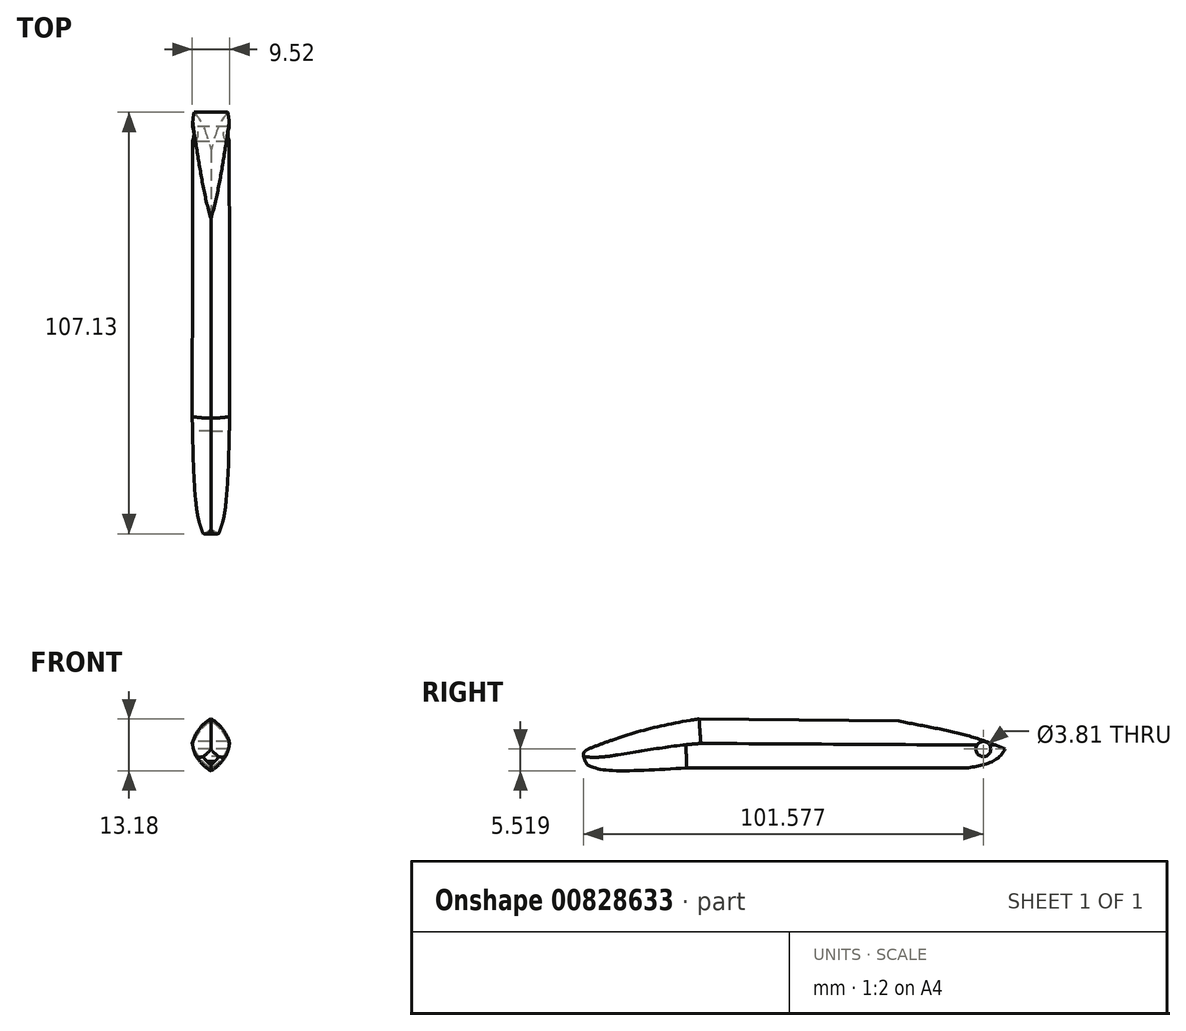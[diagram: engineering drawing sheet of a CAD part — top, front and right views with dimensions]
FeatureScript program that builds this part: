
annotation { "Feature Type Name" : "Feature", "Feature Type Description" : "" }
export const myFeature = defineFeature(function(context is Context, id is Id, definition is map)
    precondition{}
    {
        {
            var Q0;
            Q0=qCreatedBy(makeId("Right.planeOp"),FACE);
            var sketch = newSketch(context, id + "F0", { "sketchPlane" : qUnion([Q0])});
            skLineSegment(sketch, "E0.bottom", {"start": v(-19.6, 24.3) * mm, "end": v(31.2, 23.71) * mm});
            skFitSpline(sketch, "E1", {"points": [v(-19.6, 24.3) * mm, v(-36.26, 20.68) * mm, v(-47.72, 16.65) * mm], "startDerivative": vector(-31.96, -4.89) * mm, "endDerivative": vector(-23.37, -8.9) * mm});
            skFitSpline(sketch, "E2", {"points": [v(31.2, 23.71) * mm, v(49.24, 19.86) * mm, v(58.16, 16.65) * mm], "startDerivative": vector(33.9, -6.52) * mm, "endDerivative": vector(19.6, -7.94) * mm});
            skPoint(sketch, "E3.1.internal.orphan", {"position": v(55.44, 13.73) * mm});
            skFitSpline(sketch, "E4", {"points": [v(58.16, 16.65) * mm, v(55.44, 13.73) * mm, v(48.36, 11.81) * mm], "startDerivative": vector(-4.99, -9.02) * mm, "endDerivative": vector(-14.3, -2) * mm});
            skLineSegment(sketch, "E5", {"start": v(48.36, 11.81) * mm, "end": v(-22.76, 11.81) * mm});
            skFitSpline(sketch, "E6", {"points": [v(-47.95, 12.56) * mm, v(-43.68, 11.33) * mm, v(-22.76, 11.81) * mm], "startDerivative": vector(10.4, -4.36) * mm, "endDerivative": vector(35.02, 1.81) * mm});
            skFitSpline(sketch, "E7", {"points": [v(-47.95, 12.56) * mm, v(-48.51, 13.5) * mm], "startDerivative": vector(-0.94, 0.96) * mm, "endDerivative": vector(-0.94, 0.96) * mm});
            skFitSpline(sketch, "E8", {"points": [v(-47.72, 16.65) * mm, v(-48.91, 15.63) * mm, v(-48.51, 13.5) * mm], "startDerivative": vector(-3.65, -2.37) * mm, "endDerivative": vector(1.7, -4.5) * mm});
            skLineSegment(sketch, "E9", {"start": v(43.75, 21.22) * mm, "end": v(32.68, 11.81) * mm});
            skLineSegment(sketch, "E10", {"start": v(32.68, 11.81) * mm, "end": v(22.49, 23.81) * mm});
            skLineSegment(sketch, "E11", {"start": v(22.49, 23.81) * mm, "end": v(10.93, 11.81) * mm});
            skLineSegment(sketch, "E12", {"start": v(10.93, 11.81) * mm, "end": v(-1.82, 24.09) * mm});
            skLineSegment(sketch, "E13", {"start": v(-1.82, 24.09) * mm, "end": v(-13.64, 11.81) * mm});
            skLineSegment(sketch, "E14", {"start": v(-13.64, 11.81) * mm, "end": v(-21.92, 23.92) * mm});
            skLineSegment(sketch, "E15", {"start": v(-21.92, 23.92) * mm, "end": v(-30.76, 11.4) * mm});
            skLineSegment(sketch, "E16", {"start": v(-30.76, 11.4) * mm, "end": v(-41.5, 18.98) * mm});
            skLineSegment(sketch, "E17", {"start": v(-41.5, 18.98) * mm, "end": v(-46.86, 12.1) * mm});
            skCircle(sketch, "E18", {"center": v(52.6, 16.63) * mm, "radius": 1.9 * mm});
            skSolve(sketch);
        }
        {
            var Q0;
            Q0 = qSketchRegion(id + "F0", true);
            extrude(context, id + "F1", {"entities" : qUnion([Q0]), "depth" : 5.08 * mm, "offsetDistance" : 25.4 * mm});
        }
        {
            var Q0;
            Q0=makeQuery(id+"F1.opExtrude","CAP_EDGE",EDGE,{"disambiguationData":[OSD([sQuery(id+"F0.wireOp",EDGE,"E0.bottom")])],"isStart":false});
            var Q1;
            Q1=makeQuery(id+"F1.opExtrude","CAP_EDGE",EDGE,{"disambiguationData":[OSD([sQuery(id+"F0.wireOp",EDGE,"E1")])],"isStart":false});
            var Q2;
            Q2=makeQuery(id+"F1.opExtrude","CAP_EDGE",EDGE,{"disambiguationData":[OSD([sQuery(id+"F0.wireOp",EDGE,"E5")])],"isStart":false});
            var Q3;
            Q3=makeQuery(id+"F1.opExtrude","CAP_EDGE",EDGE,{"disambiguationData":[OSD([sQuery(id+"F0.wireOp",EDGE,"E6")])],"isStart":false});
            fillet(context, id + "F2", {"entities" : qUnion([Q0, Q1, Q2, Q3]), "radius" : 10.12 * mm, "tangentPropagation" : true, "allowEdgeOverflow" : false});
        }
        {
            var Q0;
            Q0=makeQuery(id+"F1.opExtrude","SWEPT_BODY",BODY,{"disambiguationData":[OSD([sQuery(id+"F0.wireOp",EDGE,"E0.bottom"),sQuery(id+"F0.wireOp",EDGE,"E1"),sQuery(id+"F0.wireOp",EDGE,"E2"),sQuery(id+"F0.wireOp",EDGE,"E4"),sQuery(id+"F0.wireOp",EDGE,"E5"),sQuery(id+"F0.wireOp",EDGE,"E6"),sQuery(id+"F0.wireOp",EDGE,"E7"),sQuery(id+"F0.wireOp",EDGE,"E8"),sQuery(id+"F0.wireOp",EDGE,"E18")])]});
            var Q1;
            {var subQ0=sQuery(id+"F0.wireOp",EDGE,"E12");Q1=makeQuery(id+"F0.imprint","IMPRINT",FACE,{"disambiguationData":[TD([[makeQuery(id+"F0.imprint","IMPRINT",EDGE,{"derivedFrom":subQ0}),1.0]])]});}
            mirror(context, id + "F3", {"operationType" : NewBodyOperationType.ADD, "entities" : qUnion([Q0]), "mirrorPlane" : qUnion([Q1])});
        }
    });
